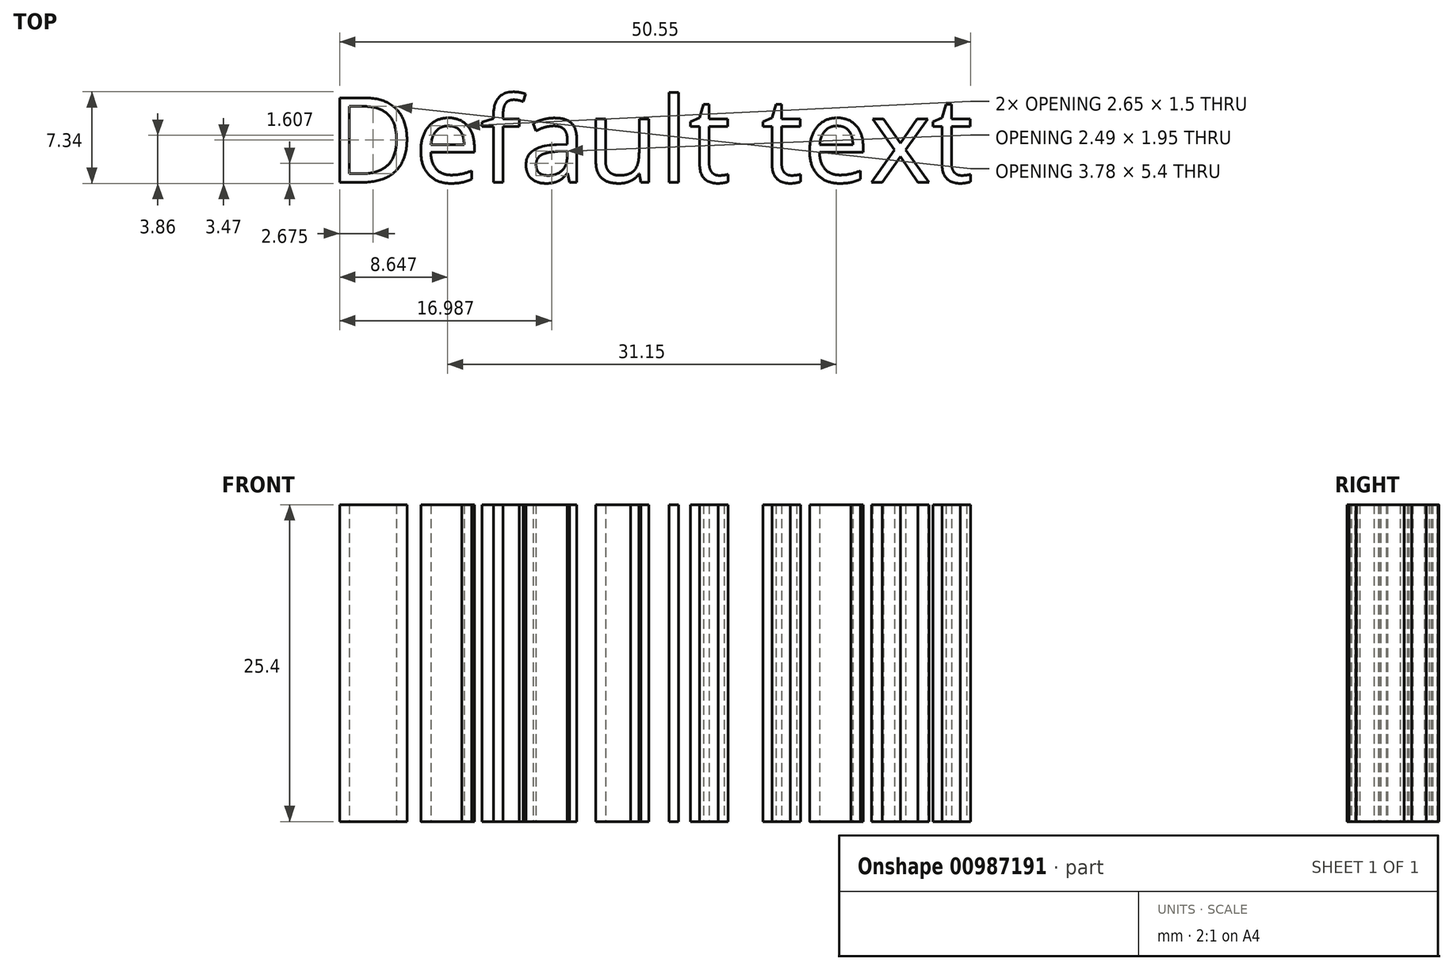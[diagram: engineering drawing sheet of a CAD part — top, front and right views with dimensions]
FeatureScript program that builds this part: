
annotation { "Feature Type Name" : "Feature", "Feature Type Description" : "" }
export const myFeature = defineFeature(function(context is Context, id is Id, definition is map)
    precondition{}
    {
        {
            var Q0;
            Q0=qCreatedBy(makeId("Top.planeOp"),FACE);
            var sketch = newSketch(context, id + "F0", { "sketchPlane" : qUnion([Q0])});
            skText(sketch, "E0", { "text": "Default text", "fontName": "OpenSans-Regular.ttf"});
            const initialGuessF0  = {"E0": [0, -0.00682, 1, 0, 0.00682]};
            skSetInitialGuess(sketch, initialGuessF0);
            skSolve(sketch);
        }
        {
            var Q0;
            Q0=qSketchRegion(id+"F0",true);
            extrude(context, id + "F1", {"entities" : qUnion([Q0]), "depth" : 25.4 * mm});
        }
    });
